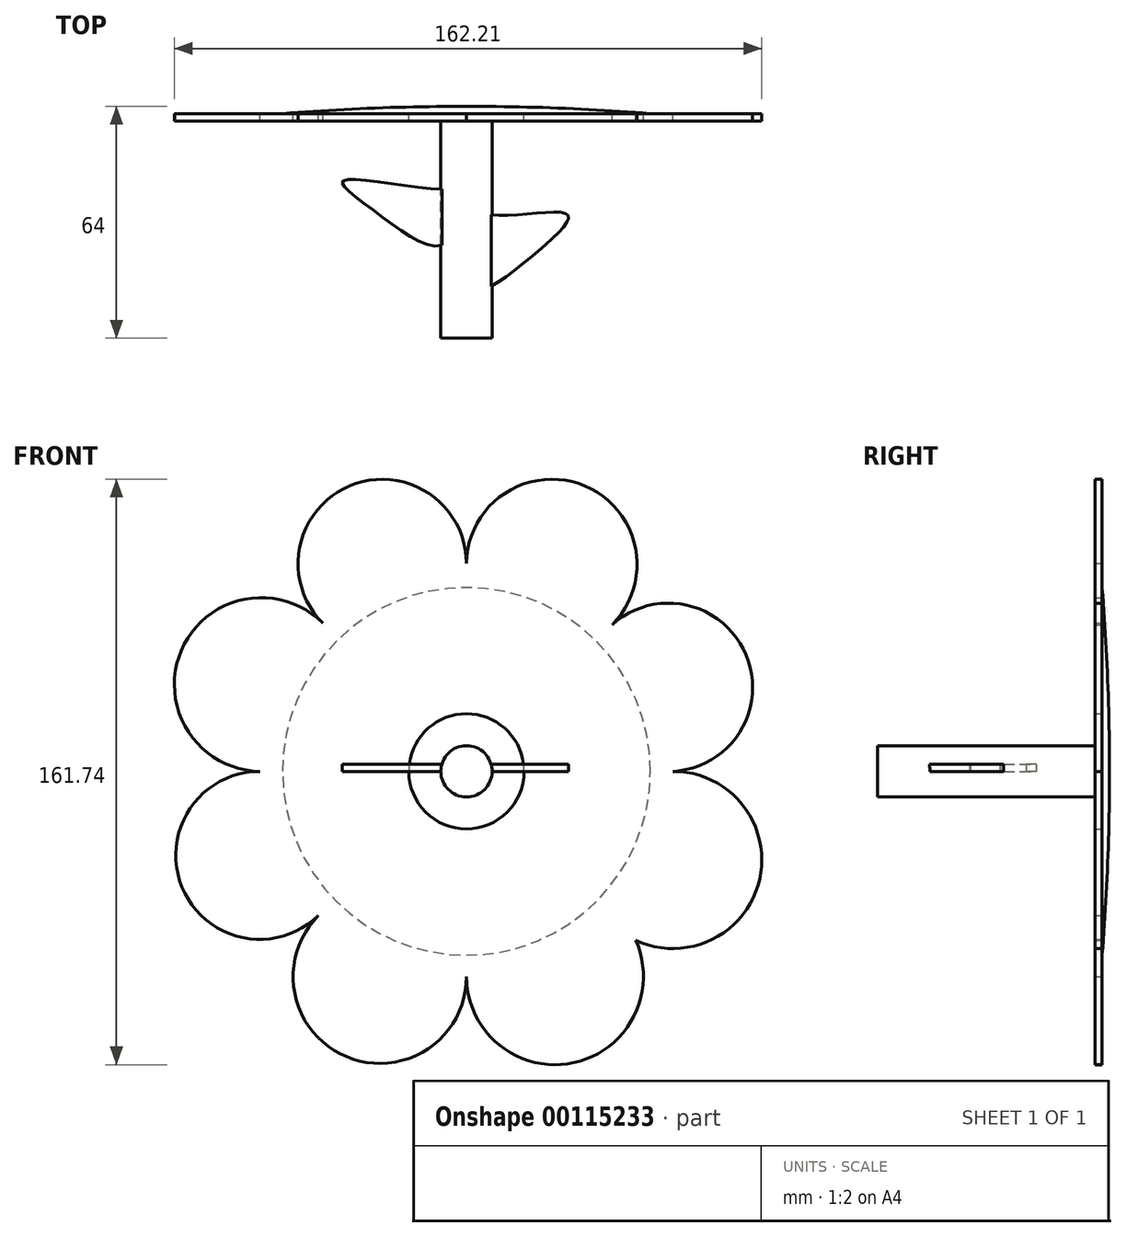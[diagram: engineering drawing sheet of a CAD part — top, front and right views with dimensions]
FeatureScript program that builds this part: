
annotation { "Feature Type Name" : "Feature", "Feature Type Description" : "" }
export const myFeature = defineFeature(function(context is Context, id is Id, definition is map)
    precondition{}
    {
        {
            var Q0;
            Q0=qCreatedBy(makeId("Front.planeOp"),FACE);
            var sketch = newSketch(context, id + "F0", { "sketchPlane" : qUnion([Q0])});
            skCircle(sketch, "E0", {"center": v(0, 0) * mm, "radius": 15.91 * mm});
            skLineSegment(sketch, "E1", {"start": v(-57.06, 0) * mm, "end": v(-15.91, 0) * mm});
            skLineSegment(sketch, "E2", {"start": v(15.91, 0) * mm, "end": v(57.07, 0) * mm});
            skLineSegment(sketch, "E3", {"start": v(0, 57.06) * mm, "end": v(0, 15.91) * mm});
            skLineSegment(sketch, "E4", {"start": v(0, -15.91) * mm, "end": v(0, -56.61) * mm});
            skLineSegment(sketch, "E5", {"start": v(11.3, -11.21) * mm, "end": v(46.74, -46.66) * mm});
            skPoint(sketch, "E6", {"position": v(40.22, 40.48) * mm});
            skPoint(sketch, "E7", {"position": v(0, 57.06) * mm});
            skLineSegment(sketch, "E8", {"start": v(40.22, 40.48) * mm, "end": v(11.12, 11.39) * mm});
            skLineSegment(sketch, "E9", {"start": v(-10.6, 11.87) * mm, "end": v(-39.7, 40.97) * mm});
            skLineSegment(sketch, "E10", {"start": v(-11.75, -10.73) * mm, "end": v(-40.85, -39.83) * mm});
            skArc(sketch, "E11", {"start": v(-57.06, 0) * mm, "mid": v(-78.56, -31.97) * mm, "end": v(-40.85, -39.83) * mm});
            skArc(sketch, "E12", {"start": v(-40.85, -39.83) * mm, "mid": v(-33.03, -78.88) * mm, "end": v(0, -56.61) * mm});
            skArc(sketch, "E13", {"start": v(0, -56.61) * mm, "mid": v(29.52, -80.5) * mm, "end": v(46.74, -46.66) * mm});
            skArc(sketch, "E14", {"start": v(-39.7, 40.97) * mm, "mid": v(-31.99, 78.96) * mm, "end": v(0, 57.06) * mm});
            skArc(sketch, "E15", {"start": v(-39.7, 40.97) * mm, "mid": v(-78.77, 33.37) * mm, "end": v(-57.06, 0) * mm});
            skArc(sketch, "E16", {"start": v(40.22, 40.48) * mm, "mid": v(32.54, 78.92) * mm, "end": v(0, 57.06) * mm});
            skArc(sketch, "E17", {"start": v(57.07, 0) * mm, "mid": v(77.25, 32.15) * mm, "end": v(40.22, 40.48) * mm});
            skArc(sketch, "E18", {"start": v(46.74, -46.66) * mm, "mid": v(80.96, -29.76) * mm, "end": v(57.07, 0) * mm});
            skSolve(sketch);
        }
        {
            var Q0;
            Q0 = qSketchRegion(id + "F0", true);
            extrude(context, id + "F1", {"entities" : qUnion([Q0]), "depth" : 2 * mm});
        }
        {
            var Q0;
            Q0=makeQuery(id+"FbSUjOW6OTPimTw_1.boolean.opBoolean","MERGE",FACE,{"derivedFrom":[makeQuery(id+"F1.opExtrude","CAP_FACE",FACE,{"disambiguationData":[OSD([sQuery(id+"F0.wireOp",EDGE,"E0"),sQuery(id+"F0.wireOp",EDGE,"E11"),sQuery(id+"F0.wireOp",EDGE,"E12"),sQuery(id+"F0.wireOp",EDGE,"E13"),sQuery(id+"F0.wireOp",EDGE,"E14"),sQuery(id+"F0.wireOp",EDGE,"E15"),sQuery(id+"F0.wireOp",EDGE,"E16"),sQuery(id+"F0.wireOp",EDGE,"E17"),sQuery(id+"F0.wireOp",EDGE,"E18")])],"isStart":true}),makeQuery(id+"FbSUjOW6OTPimTw_1.opExtrude","CAP_FACE",FACE,{"disambiguationData":[OSD([sQuery(id+"F1hUdGI8VGxZqKo_1.wireOp",EDGE,"uyr3Pzg8-eIKn-34vq-k9wb-hDaMvwdCGQYd")])],"isStart":true})]});
            var sketch = newSketch(context, id + "F2", { "sketchPlane" : qUnion([Q0])});
            skCircle(sketch, "E19", {"center": v(0, 0) * mm, "radius": 50.8 * mm});
            skSolve(sketch);
        }
        {
            var Q0;
            Q0 = qSketchRegion(id + "F2", true);
            extrude(context, id + "F3", {"entities" : qUnion([Q0]), "operationType" : NewBodyOperationType.ADD, "depth" : 2 * mm});
        }
        {
            var Q0;
            Q0=makeQuery(id+"F3.opExtrude","CAP_FACE",FACE,{"disambiguationData":[OSD([sQuery(id+"F2.wireOp",EDGE,"E19")])],"isStart":false});
            fillet(context, id + "F4", {"entities" : qUnion([Q0]), "radius" : 600 * mm, "tangentPropagation" : true, "allowEdgeOverflow" : false});
        }
        {
            var Q0;
            Q0=makeQuery(id+"F1.opExtrude","CAP_FACE",FACE,{"disambiguationData":[OSD([sQuery(id+"F0.wireOp",EDGE,"E0"),sQuery(id+"F0.wireOp",EDGE,"E11"),sQuery(id+"F0.wireOp",EDGE,"E12"),sQuery(id+"F0.wireOp",EDGE,"E13"),sQuery(id+"F0.wireOp",EDGE,"E14"),sQuery(id+"F0.wireOp",EDGE,"E15"),sQuery(id+"F0.wireOp",EDGE,"E16"),sQuery(id+"F0.wireOp",EDGE,"E17"),sQuery(id+"F0.wireOp",EDGE,"E18")])],"isStart":false});
            var sketch = newSketch(context, id + "F5", { "sketchPlane" : qUnion([Q0])});
            skSolve(sketch);
        }
        {
            var Q0;
            Q0=makeQuery(id+"F5.imprint","IMPRINT",FACE,{"disambiguationData":[TD([[makeQuery(id+"F5.imprint","IMPRINT",EDGE,{"derivedFrom":makeQuery(id+"F1.opExtrude","CAP_EDGE",EDGE,{"disambiguationData":[OSD([sQuery(id+"F0.wireOp",EDGE,"E0")])],"isStart":false})}),1.0]])]});
            var sketch = newSketch(context, id + "F6", { "sketchPlane" : qUnion([Q0])});
            skCircle(sketch, "E20", {"center": v(0, 0) * mm, "radius": 7.08 * mm});
            skSolve(sketch);
        }
        {
            var Q0;
            Q0 = qSketchRegion(id + "F6", true);
            extrude(context, id + "F7", {"entities" : qUnion([Q0]), "depth" : 60 * mm});
        }
        {
            var Q0;
            Q0=qCreatedBy(makeId("Top.planeOp"),FACE);
            var sketch = newSketch(context, id + "F8", { "sketchPlane" : qUnion([Q0])});
            skFitSpline(sketch, "E21", {"points": [v(0, -47.81) * mm, v(16.14, -41.02) * mm, v(27.86, -27.9) * mm, v(6.53, -27.9) * mm, v(0, -27.19) * mm, v(0, -47.81) * mm]});
            skFitSpline(sketch, "E22", {"points": [v(-5.36, -35.63) * mm, v(-24.1, -27.9) * mm, v(-33.95, -18.52) * mm, v(-4.65, -20.86) * mm, v(0, -20.86) * mm, v(-5.36, -35.63) * mm]});
            skSolve(sketch);
        }
        {
            var Q0;
            Q0 = qSketchRegion(id + "F8", true);
            extrude(context, id + "F9", {"entities" : qUnion([Q0]), "operationType" : NewBodyOperationType.ADD, "depth" : 2 * mm});
        }
    });
